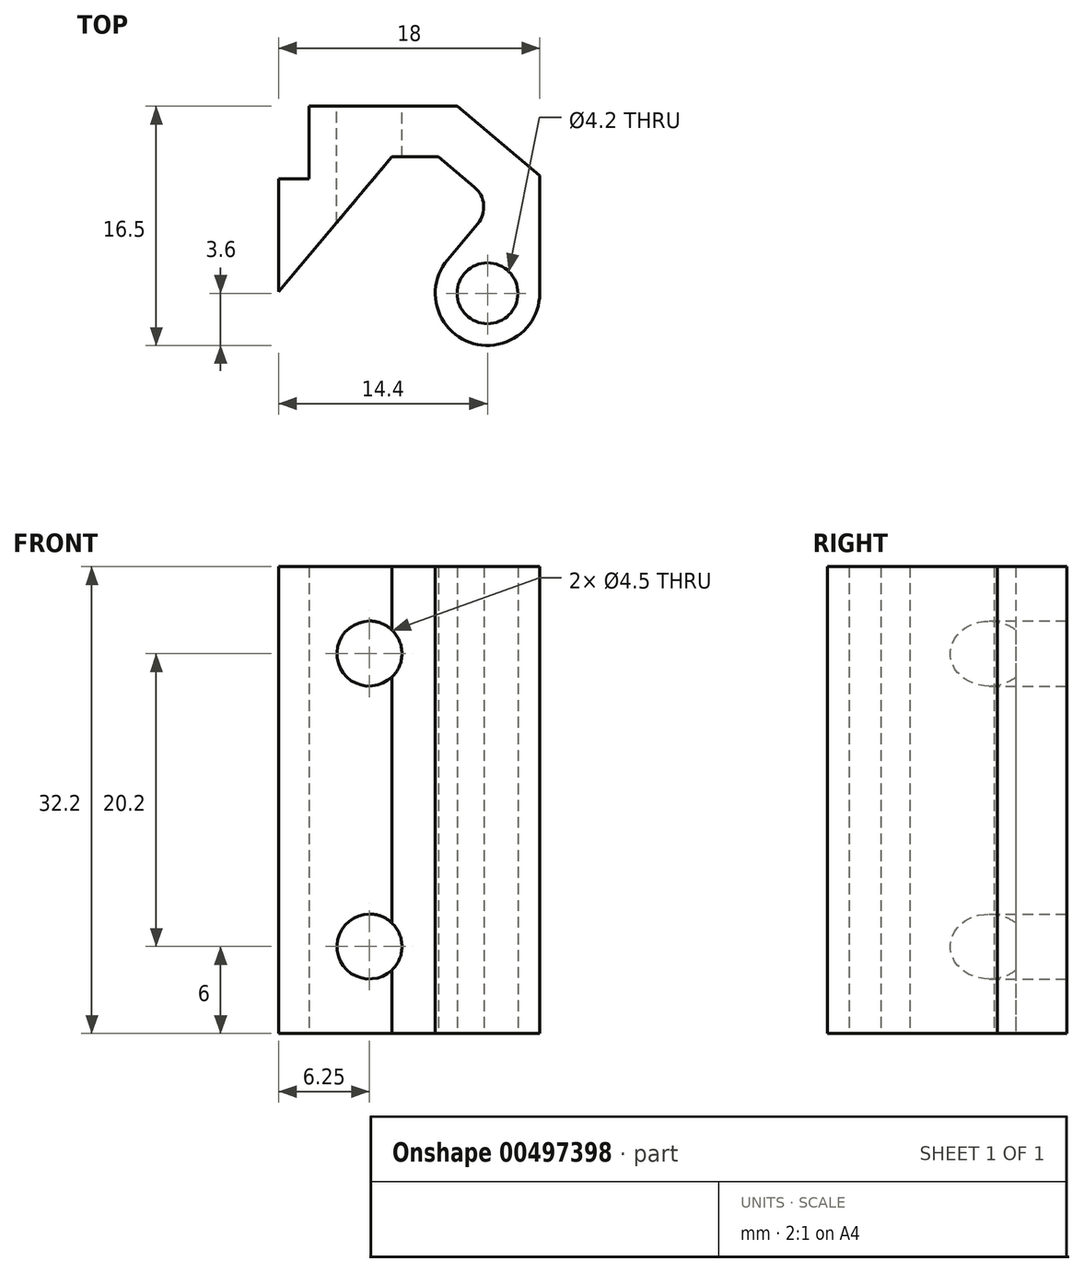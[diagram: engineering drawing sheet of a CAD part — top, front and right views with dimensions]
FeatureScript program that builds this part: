
annotation { "Feature Type Name" : "Feature", "Feature Type Description" : "" }
export const myFeature = defineFeature(function(context is Context, id is Id, definition is map)
    precondition{}
    {
        {
            var Q0;
            Q0=qCreatedBy(makeId("Top.planeOp"),FACE);
            var sketch = newSketch(context, id + "F0", { "sketchPlane" : qUnion([Q0])});
            skLineSegment(sketch, "E0", {"start": v(-18, 16.5) * mm, "end": v(-5.7, 16.5) * mm});
            skLineSegment(sketch, "E1", {"start": v(-18, 16.5) * mm, "end": v(-18, 3.7) * mm});
            skLineSegment(sketch, "E2", {"start": v(0, 16.5) * mm, "end": v(0, 0) * mm});
            skLineSegment(sketch, "E3", {"start": v(-5.7, 16.5) * mm, "end": v(0, 11.72) * mm});
            skLineSegment(sketch, "E4.0", {"start": v(-6.97, 13) * mm, "end": v(-4.5, 10.93) * mm});
            skLineSegment(sketch, "E4.1", {"start": v(-10.2, 13) * mm, "end": v(-6.97, 13) * mm});
            skCircle(sketch, "E5", {"center": v(-3.6, 3.6) * mm, "radius": 3.6 * mm});
            skLineSegment(sketch, "E6", {"start": v(-3.6, 3.6) * mm, "end": v(-3.6, 0) * mm, "construction": true});
            skPoint(sketch, "E7", {"position": v(0, 3.6) * mm});
            skLineSegment(sketch, "E8", {"start": v(-4.28, 8.39) * mm, "end": v(-6.36, 5.91) * mm});
            skLineSegment(sketch, "E9", {"start": v(-18, 3.7) * mm, "end": v(-10.2, 13) * mm});
            skPoint(sketch, "E10.visualSharp", {"position": v(-3.12, 9.77) * mm});
            skArc(sketch, "E10.filletArc", {"start": v(-4.28, 8.39) * mm, "mid": v(-3.87, 9.7) * mm, "end": v(-4.5, 10.93) * mm});
            skLineSegment(sketch, "E11", {"start": v(-15.9, 16.5) * mm, "end": v(-15.9, 11.5) * mm});
            skLineSegment(sketch, "E12", {"start": v(-15.9, 11.5) * mm, "end": v(-18, 11.5) * mm});
            skCircle(sketch, "E13", {"center": v(-3.6, 3.6) * mm, "radius": 2.1 * mm});
            skSolve(sketch);
        }
        {
            var Q0;
            {var subQ5=sQuery(id+"F0.wireOp",EDGE,"E3");Q0=makeQuery(id+"F0.imprint","IMPRINT",FACE,{"disambiguationData":[TD([[makeQuery(id+"F0.imprint","IMPRINT",EDGE,{"derivedFrom":subQ5}),-1.0]])]});}
            var Q1;
            Q1=makeQuery(id+"F0.imprint","IMPRINT",FACE,{"disambiguationData":[TD([[makeQuery(id+"F0.imprint","IMPRINT",EDGE,{"derivedFrom":sQuery(id+"F0.wireOp",EDGE,"E13")}),-1.0]])]});
            extrude(context, id + "F1", {"entities" : qUnion([Q0, Q1]), "depth" : 32.2 * mm});
        }
        {
            var Q0;
            Q0=makeQuery(id+"F1.opExtrude","SWEPT_FACE",FACE,{"disambiguationData":[OSD([sQuery(id+"F0.wireOp",EDGE,"E0")])]});
            var sketch = newSketch(context, id + "F2", { "sketchPlane" : qUnion([Q0])});
            skCircle(sketch, "E14", {"center": v(11.75, 26.2) * mm, "radius": 2.25 * mm});
            skCircle(sketch, "E15", {"center": v(11.75, 6) * mm, "radius": 2.25 * mm});
            skLineSegment(sketch, "E16", {"start": v(7.23, 32.2) * mm, "end": v(7.23, 0) * mm, "construction": true});
            skPoint(sketch, "E17", {"position": v(7.23, 16.1) * mm});
            skLineSegment(sketch, "E18", {"start": v(11.75, 26.2) * mm, "end": v(11.75, 6) * mm, "construction": true});
            skPoint(sketch, "E19", {"position": v(11.75, 16.1) * mm});
            skSolve(sketch);
        }
        {
            var Q0;
            Q0=makeQuery(id+"F2.imprint","IMPRINT",FACE,{"disambiguationData":[TD([[makeQuery(id+"F2.imprint","IMPRINT",EDGE,{"derivedFrom":sQuery(id+"F2.wireOp",EDGE,"E14")}),1.0]])]});
            var Q1;
            Q1=makeQuery(id+"F2.imprint","IMPRINT",FACE,{"disambiguationData":[TD([[makeQuery(id+"F2.imprint","IMPRINT",EDGE,{"derivedFrom":sQuery(id+"F2.wireOp",EDGE,"E15")}),1.0]])]});
            extrude(context, id + "F3", {"entities" : qUnion([Q0, Q1]), "operationType" : NewBodyOperationType.REMOVE, "endBound" : BoundingType.THROUGH_ALL, "oppositeDirection" : true, "depth" : 25 * mm});
        }
    });
